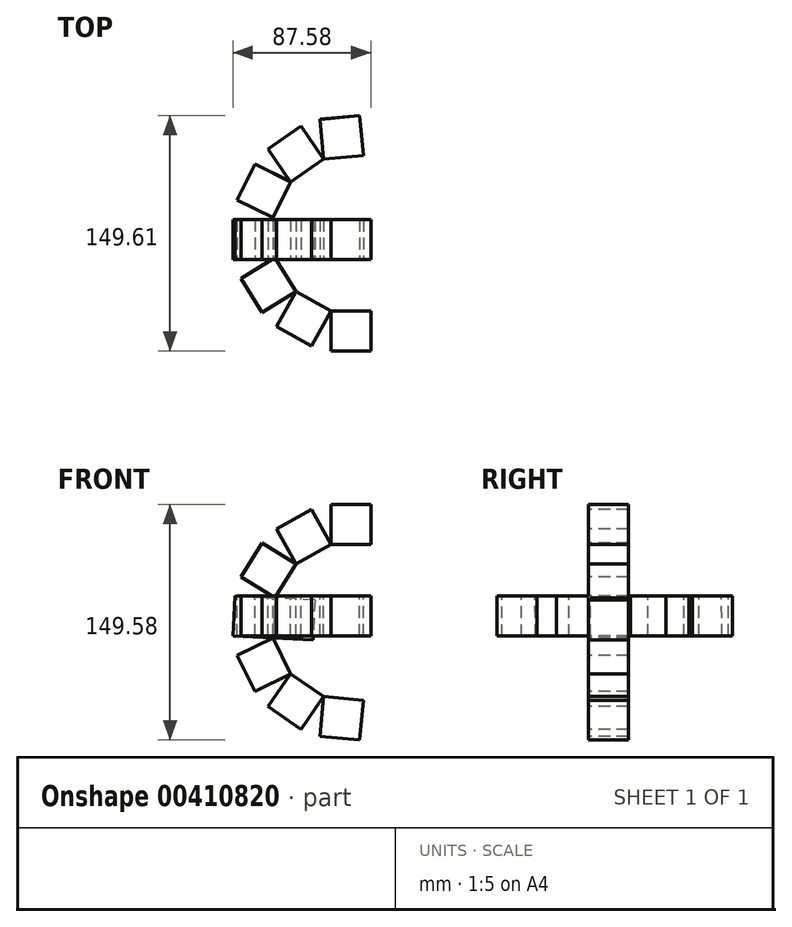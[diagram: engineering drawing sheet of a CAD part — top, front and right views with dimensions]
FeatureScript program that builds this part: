
annotation { "Feature Type Name" : "Feature", "Feature Type Description" : "" }
export const myFeature = defineFeature(function(context is Context, id is Id, definition is map)
    precondition{}
    {
        {
            var Q0;
            Q0=qCreatedBy(makeId("Front.planeOp"),FACE);
            var sketch = newSketch(context, id + "F0", { "sketchPlane" : qUnion([Q0])});
            skLineSegment(sketch, "E0", {"start": v(-22.82, -14.72) * mm, "end": v(2.58, -14.72) * mm});
            skLineSegment(sketch, "E1", {"start": v(2.58, -14.72) * mm, "end": v(24.78, -27.07) * mm});
            skLineSegment(sketch, "E2", {"start": v(2.58, -14.72) * mm, "end": v(2.58, -14.72) * mm});
            skPoint(sketch, "E3", {"position": v(-10.12, -14.72) * mm});
            skLineSegment(sketch, "E4", {"start": v(-10.12, -14.72) * mm, "end": v(-10.12, -39.19) * mm});
            skLineSegment(sketch, "E5.MirrorCS", {"start": v(-22.82, -14.72) * mm, "end": v(-45.02, -27.07) * mm});
            skLineSegment(sketch, "E6.MirrorCS", {"start": v(-22.82, -14.72) * mm, "end": v(-22.82, -14.72) * mm});
            skPoint(sketch, "E7", {"position": v(-33.92, -20.9) * mm});
            skPoint(sketch, "E8", {"position": v(13.68, -20.9) * mm});
            skLineSegment(sketch, "E9", {"start": v(-33.92, -20.9) * mm, "end": v(-19.57, -46.68) * mm});
            skLineSegment(sketch, "E10", {"start": v(13.68, -20.9) * mm, "end": v(-1.9, -48.91) * mm});
            skLineSegment(sketch, "E11.MirrorCS", {"start": v(-45.02, -27.07) * mm, "end": v(-45.02, -27.07) * mm});
            skLineSegment(sketch, "E12.MirrorCS", {"start": v(-45.02, -27.07) * mm, "end": v(-58.41, -48.65) * mm});
            skLineSegment(sketch, "E13.MirrorCS", {"start": v(-58.41, -48.65) * mm, "end": v(-58.41, -48.65) * mm});
            skLineSegment(sketch, "E14.MirrorCS", {"start": v(-58.41, -48.65) * mm, "end": v(-59.63, -74.02) * mm});
            skLineSegment(sketch, "E15.MirrorCS", {"start": v(-59.02, -61.33) * mm, "end": v(-27, -62.87) * mm});
            skLineSegment(sketch, "E16.MirrorCS", {"start": v(-51.71, -37.86) * mm, "end": v(-30.93, -50.76) * mm});
            skLineSegment(sketch, "E17.MirrorCS", {"start": v(-59.63, -74.02) * mm, "end": v(-59.63, -74.02) * mm});
            skLineSegment(sketch, "E18.MirrorCS", {"start": v(-48.35, -96.78) * mm, "end": v(-59.63, -74.02) * mm});
            skLineSegment(sketch, "E19.MirrorCS", {"start": v(-53.99, -85.4) * mm, "end": v(-32.06, -74.54) * mm});
            skLineSegment(sketch, "E20.MirrorCS", {"start": v(-48.35, -96.78) * mm, "end": v(-48.35, -96.78) * mm});
            skLineSegment(sketch, "E21.MirrorCS", {"start": v(-27.44, -111.2) * mm, "end": v(-48.35, -96.78) * mm});
            skLineSegment(sketch, "E22.MirrorCS", {"start": v(-37.9, -103.99) * mm, "end": v(-21.15, -79.69) * mm});
            skLineSegment(sketch, "E23.MirrorCS", {"start": v(-27.44, -111.2) * mm, "end": v(-2.15, -113.62) * mm});
            skLineSegment(sketch, "E24.MirrorCS", {"start": v(-14.8, -112.4) * mm, "end": v(-12.46, -88.05) * mm});
            skLineSegment(sketch, "E25.MirrorCS", {"start": v(-27.44, -111.2) * mm, "end": v(-27.44, -111.2) * mm});
            skLineSegment(sketch, "E26.MirrorCS", {"start": v(-2.15, -113.62) * mm, "end": v(21.12, -103.45) * mm});
            skLineSegment(sketch, "E27.MirrorCS", {"start": v(-2.15, -113.62) * mm, "end": v(-2.15, -113.62) * mm});
            skPoint(sketch, "E28", {"position": v(9.48, -108.53) * mm});
            skLineSegment(sketch, "E29.MirrorCS", {"start": v(9.48, -108.53) * mm, "end": v(-2.33, -81.5) * mm});
            skLineSegment(sketch, "E30.MirrorCS", {"start": v(28.82, -93.34) * mm, "end": v(9.36, -78.52) * mm});
            skLineSegment(sketch, "E31.MirrorCS", {"start": v(38.33, -70.67) * mm, "end": v(6.6, -66.09) * mm});
            skLineSegment(sketch, "E32.MirrorCS", {"start": v(35.62, -46.24) * mm, "end": v(12.76, -54.95) * mm});
            skLineSegment(sketch, "E33.MirrorCS", {"start": v(40.15, -58.1) * mm, "end": v(36.52, -83.24) * mm});
            skLineSegment(sketch, "E34.MirrorCS", {"start": v(31.1, -34.37) * mm, "end": v(40.15, -58.1) * mm});
            skLineSegment(sketch, "E35.MirrorCS", {"start": v(11.65, -18.03) * mm, "end": v(31.1, -34.37) * mm});
            skLineSegment(sketch, "E36.MirrorCS", {"start": v(21.12, -103.45) * mm, "end": v(36.52, -83.24) * mm});
            skLineSegment(sketch, "E37.MirrorCS", {"start": v(36.52, -83.24) * mm, "end": v(36.52, -83.24) * mm});
            skLineSegment(sketch, "E38.MirrorCS", {"start": v(40.15, -58.1) * mm, "end": v(40.15, -58.1) * mm});
            skLineSegment(sketch, "E39.MirrorCS", {"start": v(31.1, -34.37) * mm, "end": v(31.1, -34.37) * mm});
            skLineSegment(sketch, "E40.MirrorCS", {"start": v(21.12, -103.45) * mm, "end": v(21.12, -103.45) * mm});
            skSolve(sketch);
        }
        {
            var Q0;
            Q0=sQuery(id+"F0.wireOp",EDGE,"E0");
            var Q1;
            Q1=sQuery(id+"F0.wireOp",EDGE,"E5.MirrorCS");
            var Q2;
            Q2=sQuery(id+"F0.wireOp",EDGE,"E12.MirrorCS");
            var Q3;
            Q3=sQuery(id+"F0.wireOp",EDGE,"E14.MirrorCS");
            var Q4;
            Q4=sQuery(id+"F0.wireOp",EDGE,"E18.MirrorCS");
            var Q5;
            Q5=sQuery(id+"F0.wireOp",EDGE,"E21.MirrorCS");
            var Q6;
            Q6=sQuery(id+"F0.wireOp",EDGE,"E23.MirrorCS");
            var Q7;
            Q7=sQuery(id+"F0.wireOp",EDGE,"E26.MirrorCS");
            var Q8;
            Q8=sQuery(id+"F0.wireOp",EDGE,"E36.MirrorCS");
            var Q9;
            Q9=sQuery(id+"F0.wireOp",EDGE,"E33.MirrorCS");
            var Q10;
            Q10=sQuery(id+"F0.wireOp",EDGE,"E34.MirrorCS");
            var Q11;
            Q11=sQuery(id+"F0.wireOp",EDGE,"E35.MirrorCS");
            extrude(context, id + "F1", {"bodyType" : ToolBodyType.SURFACE, "surfaceEntities" : qUnion([Q0, Q1, Q2, Q3, Q4, Q5, Q6, Q7, Q8, Q9, Q10, Q11]), "endBound" : BoundingType.SYMMETRIC, "depth" : 25.4 * mm});
        }
        {
            var Q0;
            Q0=makeQuery(id+"F1.opExtrude","SWEPT_FACE",FACE,{"disambiguationData":[OSD([sQuery(id+"F0.wireOp",EDGE,"E14.MirrorCS")])]});
            extrude(context, id + "F2", {"entities" : qUnion([Q0]), "depth" : 25.4 * mm});
        }
        {
            var Q0;
            Q0=makeQuery(id+"F1.opExtrude","SWEPT_FACE",FACE,{"disambiguationData":[OSD([sQuery(id+"F0.wireOp",EDGE,"E18.MirrorCS")])]});
            extrude(context, id + "F3", {"entities" : qUnion([Q0]), "oppositeDirection" : true, "depth" : 25.4 * mm});
        }
        {
            var Q0;
            Q0=makeQuery(id+"F1.opExtrude","SWEPT_FACE",FACE,{"disambiguationData":[OSD([sQuery(id+"F0.wireOp",EDGE,"E12.MirrorCS")])]});
            extrude(context, id + "F4", {"entities" : qUnion([Q0]), "oppositeDirection" : true, "depth" : 25.4 * mm});
        }
        {
            var Q0;
            Q0=makeQuery(id+"F1.opExtrude","SWEPT_FACE",FACE,{"disambiguationData":[OSD([sQuery(id+"F0.wireOp",EDGE,"E5.MirrorCS")])]});
            extrude(context, id + "F5", {"entities" : qUnion([Q0]), "oppositeDirection" : true, "depth" : 25.4 * mm});
        }
        {
            var Q0;
            Q0=makeQuery(id+"F1.opExtrude","SWEPT_FACE",FACE,{"disambiguationData":[OSD([sQuery(id+"F0.wireOp",EDGE,"E0")])]});
            extrude(context, id + "F6", {"entities" : qUnion([Q0]), "oppositeDirection" : true, "depth" : 25.4 * mm});
        }
        {
            var Q0;
            Q0=makeQuery(id+"F1.opExtrude","SWEPT_FACE",FACE,{"disambiguationData":[OSD([sQuery(id+"F0.wireOp",EDGE,"E21.MirrorCS")])]});
            extrude(context, id + "F7", {"entities" : qUnion([Q0]), "oppositeDirection" : true, "depth" : 25.4 * mm});
        }
        {
            var Q0;
            Q0=makeQuery(id+"F1.opExtrude","SWEPT_FACE",FACE,{"disambiguationData":[OSD([sQuery(id+"F0.wireOp",EDGE,"E23.MirrorCS")])]});
            extrude(context, id + "F8", {"entities" : qUnion([Q0]), "oppositeDirection" : true, "depth" : 25.4 * mm});
        }
        {
            var Q0;
            Q0=makeQuery(id+"F1.opExtrude","SWEPT_FACE",FACE,{"disambiguationData":[OSD([sQuery(id+"F0.wireOp",EDGE,"E14.MirrorCS")])]});
            extrude(context, id + "F9", {"entities" : qUnion([Q0]), "oppositeDirection" : true, "depth" : 25.4 * mm});
        }
        {
            var Q0;
            Q0=makeQuery(id+"F1.opExtrude","SWEPT_FACE",FACE,{"disambiguationData":[OSD([sQuery(id+"F0.wireOp",EDGE,"E18.MirrorCS")])]});
            extrude(context, id + "F10", {"entities" : qUnion([Q0]), "oppositeDirection" : true, "depth" : 25.4 * mm});
        }
        {
            var Q0;
            Q0=makeQuery(id+"F9.opExtrude","CAP_FACE",FACE,{"disambiguationData":[OSD([sQuery(id+"F0.wireOp",EDGE,"E14.MirrorCS")])],"isStart":false});
            var sketch = newSketch(context, id + "F11", { "sketchPlane" : qUnion([Q0])});
            skLineSegment(sketch, "E41", {"start": v(-0.5, -76.79) * mm, "end": v(0, -51.39) * mm});
            skLineSegment(sketch, "E42", {"start": v(12.7, -64.09) * mm, "end": v(-12.7, -64.09) * mm});
            skLineSegment(sketch, "E43", {"start": v(-12.7, -51.39) * mm, "end": v(12.7, -76.79) * mm});
            skLineSegment(sketch, "E44", {"start": v(-12.7, -76.79) * mm, "end": v(12.7, -51.39) * mm});
            skSolve(sketch);
        }
        {
            var Q0;
            Q0=sQuery(id+"F11.wireOp",EDGE,"E44");
            cPlane(context, id + "F12", {"entities" : qUnion([Q0]), "cplaneType" : CPlaneType.LINE_ANGLE, "offset" : 25.4 * mm, "angle" : 0 * degree, "width" : 152.4 * mm, "height" : 152.4 * mm});
        }
        {
            var Q0;
            Q0=makeQuery(id+"F10.opExtrude","SWEPT_BODY",BODY,{"disambiguationData":[OSD([sQuery(id+"F0.wireOp",EDGE,"E18.MirrorCS")])]});
            var Q1;
            Q1=makeQuery(id+"F8.opExtrude","SWEPT_BODY",BODY,{"disambiguationData":[OSD([sQuery(id+"F0.wireOp",EDGE,"E23.MirrorCS")])]});
            var Q2;
            Q2=makeQuery(id+"F7.opExtrude","SWEPT_BODY",BODY,{"disambiguationData":[OSD([sQuery(id+"F0.wireOp",EDGE,"E21.MirrorCS")])]});
            var Q3;
            Q3=makeQuery(id+"F6.opExtrude","SWEPT_BODY",BODY,{"disambiguationData":[OSD([sQuery(id+"F0.wireOp",EDGE,"E0")])]});
            var Q4;
            Q4=makeQuery(id+"F5.opExtrude","SWEPT_BODY",BODY,{"disambiguationData":[OSD([sQuery(id+"F0.wireOp",EDGE,"E5.MirrorCS")])]});
            var Q5;
            Q5=makeQuery(id+"F4.opExtrude","SWEPT_BODY",BODY,{"disambiguationData":[OSD([sQuery(id+"F0.wireOp",EDGE,"E12.MirrorCS")])]});
            var Q6;
            Q6=qCreatedBy(id+"F12.planeOp",FACE);
            mirror(context, id + "F13", {"entities" : qUnion([Q0, Q1, Q2, Q3, Q4, Q5]), "mirrorPlane" : qUnion([Q6])});
        }
    });
